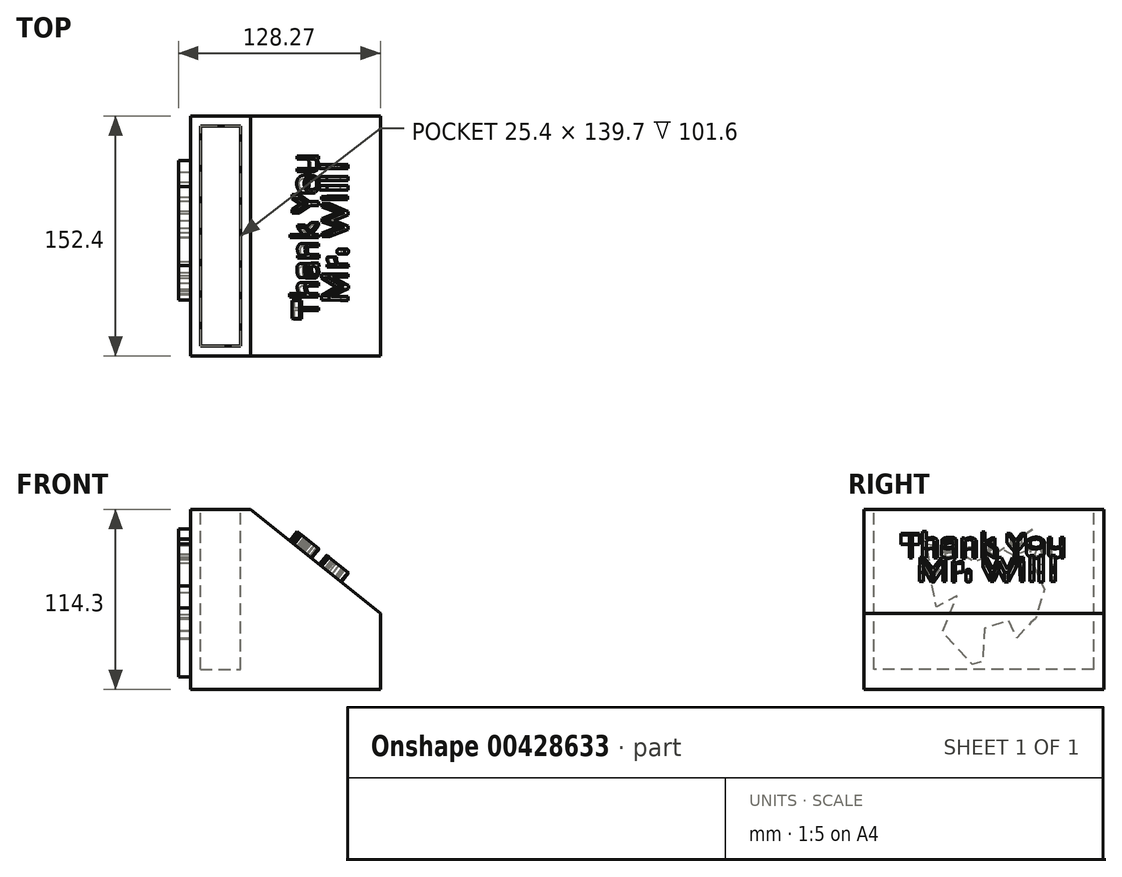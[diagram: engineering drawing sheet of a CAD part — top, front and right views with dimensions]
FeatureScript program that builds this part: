
annotation { "Feature Type Name" : "Feature", "Feature Type Description" : "" }
export const myFeature = defineFeature(function(context is Context, id is Id, definition is map)
    precondition{}
    {
        {
            var Q0;
            Q0=qCreatedBy(makeId("Front.planeOp"),FACE);
            var sketch = newSketch(context, id + "F0", { "sketchPlane" : qUnion([Q0])});
            skLineSegment(sketch, "E0.bottom", {"start": v(-51.92, 36.98) * mm, "end": v(-13.82, 36.98) * mm});
            skLineSegment(sketch, "E0.top", {"start": v(-51.92, -77.32) * mm, "end": v(-13.82, -77.32) * mm});
            skLineSegment(sketch, "E0.left", {"start": v(-51.92, 36.98) * mm, "end": v(-51.92, -77.32) * mm});
            skLineSegment(sketch, "E0.right", {"start": v(-13.82, 36.98) * mm, "end": v(-13.82, -77.32) * mm});
            skLineSegment(sketch, "E1", {"start": v(68.73, -77.32) * mm, "end": v(-13.82, -77.32) * mm});
            skLineSegment(sketch, "E2", {"start": v(68.73, -77.32) * mm, "end": v(68.73, -29.16) * mm});
            skLineSegment(sketch, "E3", {"start": v(68.73, -29.16) * mm, "end": v(-13.82, 36.98) * mm});
            skSolve(sketch);
        }
        {
            var Q0;
            Q0=makeQuery(id+"F0.imprint","IMPRINT",FACE,{"disambiguationData":[TD([[makeQuery(id+"F0.imprint","IMPRINT",EDGE,{"derivedFrom":sQuery(id+"F0.wireOp",EDGE,"E0.bottom")}),-1.0]])]});
            var Q1;
            Q1=makeQuery(id+"F0.imprint","IMPRINT",FACE,{"disambiguationData":[TD([[makeQuery(id+"F0.imprint","IMPRINT",EDGE,{"derivedFrom":sQuery(id+"F0.wireOp",EDGE,"E0.right")}),1.0]])]});
            extrude(context, id + "F1", {"entities" : qUnion([Q0, Q1]), "depth" : 152.4 * mm});
        }
        {
            var Q0;
            Q0=makeQuery(id+"F1.opExtrude","SWEPT_FACE",FACE,{"disambiguationData":[OSD([sQuery(id+"F0.wireOp",EDGE,"E0.bottom")])]});
            var sketch = newSketch(context, id + "F2", { "sketchPlane" : qUnion([Q0])});
            skLineSegment(sketch, "E4", {"start": v(-51.92, 0) * mm, "end": v(-51.92, -50.8) * mm});
            skPoint(sketch, "E5.centerSnap0", {"position": v(-32.87, 0) * mm});
            skPoint(sketch, "E5.centerSnap1", {"position": v(-51.92, -25.4) * mm});
            skLineSegment(sketch, "E6", {"start": v(-51.92, -50.8) * mm, "end": v(-51.92, -101.6) * mm});
            skPoint(sketch, "E7.centerSnap0", {"position": v(-51.92, -76.2) * mm});
            skLineSegment(sketch, "E8", {"start": v(-51.92, -101.6) * mm, "end": v(-51.92, -152.4) * mm});
            skPoint(sketch, "E9.centerSnap0", {"position": v(-51.92, -127) * mm});
            skPoint(sketch, "E10.startSnap0", {"position": v(-32.87, -152.4) * mm});
            skLineSegment(sketch, "E11", {"start": v(-45.57, -6.35) * mm, "end": v(-45.57, -146.05) * mm});
            skLineSegment(sketch, "E12", {"start": v(-20.17, -146.05) * mm, "end": v(-20.17, -6.35) * mm});
            skLineSegment(sketch, "E13", {"start": v(-45.57, -6.35) * mm, "end": v(-20.17, -6.35) * mm});
            skLineSegment(sketch, "E14", {"start": v(-45.57, -146.05) * mm, "end": v(-20.17, -146.05) * mm});
            skSolve(sketch);
        }
        {
            var Q0;
            Q0=makeQuery(id+"F1.opExtrude","SWEPT_FACE",FACE,{"disambiguationData":[OSD([sQuery(id+"F0.wireOp",EDGE,"E3")])]});
            var sketch = newSketch(context, id + "F3", { "sketchPlane" : qUnion([Q0])});
            skLineSegment(sketch, "E15", {"start": v(0, -128.67) * mm, "end": v(0, -117.04) * mm});
            skLineSegment(sketch, "E16", {"start": v(0, -117.04) * mm, "end": v(1.55, -117.04) * mm});
            skLineSegment(sketch, "E17", {"start": v(1.55, -117.04) * mm, "end": v(1.55, -121.65) * mm});
            skLineSegment(sketch, "E18", {"start": v(1.55, -121.65) * mm, "end": v(15.42, -121.65) * mm});
            skLineSegment(sketch, "E19", {"start": v(15.42, -121.65) * mm, "end": v(15.42, -123.54) * mm});
            skLineSegment(sketch, "E20", {"start": v(15.42, -123.54) * mm, "end": v(1.55, -123.54) * mm});
            skLineSegment(sketch, "E21", {"start": v(1.55, -123.54) * mm, "end": v(1.55, -128.78) * mm});
            skLineSegment(sketch, "E22", {"start": v(1.55, -128.78) * mm, "end": v(0, -128.67) * mm});
            skLineSegment(sketch, "E23", {"start": v(-1.97, -115.05) * mm, "end": v(15.11, -115.05) * mm});
            skLineSegment(sketch, "E24", {"start": v(15.11, -115.05) * mm, "end": v(15.11, -112.72) * mm});
            skFitSpline(sketch, "E25", {"points": [v(5.82, -112.75) * mm, v(4.64, -111.39) * mm, v(4.22, -109.92) * mm, v(4.22, -107.83) * mm, v(5.92, -106.05) * mm, v(7.53, -105.73) * mm], "startDerivative": vector(-5.14, 7.22) * mm, "endDerivative": vector(8.33, 0.38) * mm});
            skLineSegment(sketch, "E26", {"start": v(7.85, -112.75) * mm, "end": v(15.11, -112.75) * mm});
            skLineSegment(sketch, "E27", {"start": v(-1.97, -115.05) * mm, "end": v(-1.97, -112.65) * mm});
            skLineSegment(sketch, "E28", {"start": v(-1.97, -112.65) * mm, "end": v(5.82, -112.75) * mm});
            skLineSegment(sketch, "E29", {"start": v(7.53, -105.73) * mm, "end": v(15.53, -105.73) * mm});
            skLineSegment(sketch, "E30", {"start": v(15.53, -105.73) * mm, "end": v(15.53, -107.93) * mm});
            skLineSegment(sketch, "E31", {"start": v(15.53, -107.93) * mm, "end": v(7.53, -107.93) * mm});
            skFitSpline(sketch, "E32", {"points": [v(7.85, -112.75) * mm, v(6.56, -111.5) * mm, v(5.82, -109.5) * mm, v(7.53, -107.93) * mm], "startDerivative": vector(-3.95, 3.77) * mm, "endDerivative": vector(7.86, 4.5) * mm});
            skLineSegment(sketch, "E33", {"start": v(8.58, -75.32) * mm, "end": v(4.47, -70.95) * mm});
            skLineSegment(sketch, "E34", {"start": v(4.47, -70.95) * mm, "end": v(4.47, -69.17) * mm});
            skLineSegment(sketch, "E35", {"start": v(8.58, -73.2) * mm, "end": v(4.47, -69.17) * mm});
            skLineSegment(sketch, "E36", {"start": v(8.58, -73.2) * mm, "end": v(15.22, -67.5) * mm});
            skLineSegment(sketch, "E37", {"start": v(15.22, -67.5) * mm, "end": v(15.22, -69.43) * mm});
            skLineSegment(sketch, "E38", {"start": v(15.22, -69.43) * mm, "end": v(9.52, -75.23) * mm});
            skLineSegment(sketch, "E39", {"start": v(9.52, -75.23) * mm, "end": v(15.52, -75.23) * mm});
            skLineSegment(sketch, "E40", {"start": v(15.52, -75.23) * mm, "end": v(15.52, -77.3) * mm});
            skLineSegment(sketch, "E41", {"start": v(15.52, -77.3) * mm, "end": v(-1.78, -77.3) * mm});
            skLineSegment(sketch, "E42", {"start": v(-1.78, -77.3) * mm, "end": v(-1.78, -75.32) * mm});
            skLineSegment(sketch, "E43", {"start": v(4.36, -90.13) * mm, "end": v(15.63, -90.13) * mm});
            skLineSegment(sketch, "E44", {"start": v(15.63, -90.13) * mm, "end": v(15.63, -87.94) * mm});
            skLineSegment(sketch, "E45", {"start": v(15.63, -87.94) * mm, "end": v(8.58, -87.94) * mm});
            skLineSegment(sketch, "E46", {"start": v(4.36, -90.13) * mm, "end": v(4.36, -88.49) * mm});
            skLineSegment(sketch, "E47", {"start": v(4.36, -88.49) * mm, "end": v(5.7, -88.49) * mm});
            skFitSpline(sketch, "E48", {"points": [v(5.7, -88.49) * mm, v(4.7, -86.62) * mm, v(4.25, -84.1) * mm, v(5.7, -81.7) * mm, v(7.49, -80.81) * mm], "startDerivative": vector(-4.46, 7.44) * mm, "endDerivative": vector(7.96, 2.67) * mm});
            skLineSegment(sketch, "E49", {"start": v(7.49, -80.81) * mm, "end": v(15.52, -80.81) * mm});
            skPoint(sketch, "E49.endSnap0", {"position": v(15.52, -76.27) * mm});
            skLineSegment(sketch, "E50", {"start": v(15.52, -80.81) * mm, "end": v(15.52, -83) * mm});
            skLineSegment(sketch, "E51", {"start": v(15.52, -83) * mm, "end": v(7.49, -83) * mm});
            skFitSpline(sketch, "E52", {"points": [v(7.49, -83) * mm, v(6.6, -84) * mm, v(6.26, -85.42) * mm, v(8.58, -87.94) * mm], "startDerivative": vector(-3.47, -3.28) * mm, "endDerivative": vector(11.5, -2.26) * mm});
            skFitSpline(sketch, "E53", {"points": [v(5.59, -102.51) * mm, v(4.82, -101.63) * mm, v(4.25, -100.1) * mm, v(4.14, -95.61) * mm, v(6.26, -93.53) * mm], "startDerivative": vector(-0.62, 6.93) * mm, "endDerivative": vector(8.79, 5.04) * mm});
            skFitSpline(sketch, "E54", {"points": [v(5.59, -102.51) * mm, v(6.82, -102.51) * mm, v(6.06, -100.44) * mm, v(5.59, -98.46) * mm, v(6.37, -96.05) * mm, v(8.38, -95.94) * mm, v(8.6, -99.89) * mm, v(10.45, -102.51) * mm, v(12.62, -102.96) * mm, v(15.3, -100.76) * mm, v(15.41, -97.37) * mm, v(14.4, -95.5) * mm], "startDerivative": vector(28.37, -7.23) * mm, "endDerivative": vector(-13.83, 20.1) * mm});
            skLineSegment(sketch, "E55", {"start": v(14.4, -95.5) * mm, "end": v(15.63, -95.5) * mm});
            skLineSegment(sketch, "E56", {"start": v(15.63, -95.5) * mm, "end": v(15.41, -93.42) * mm});
            skLineSegment(sketch, "E57", {"start": v(15.41, -93.42) * mm, "end": v(6.26, -93.53) * mm});
            skLineSegment(sketch, "E58", {"start": v(0, -61.47) * mm, "end": v(0, -59.24) * mm});
            skLineSegment(sketch, "E59", {"start": v(0, -52.37) * mm, "end": v(0, -49.75) * mm});
            skLineSegment(sketch, "E60", {"start": v(0, -49.75) * mm, "end": v(8.14, -54.4) * mm});
            skLineSegment(sketch, "E61", {"start": v(8.14, -54.4) * mm, "end": v(15.33, -54.4) * mm});
            skLineSegment(sketch, "E62", {"start": v(15.33, -54.4) * mm, "end": v(15.33, -56.72) * mm});
            skLineSegment(sketch, "E63", {"start": v(15.33, -56.72) * mm, "end": v(9.03, -56.72) * mm});
            skLineSegment(sketch, "E64", {"start": v(9.03, -56.72) * mm, "end": v(0, -61.47) * mm});
            skLineSegment(sketch, "E65", {"start": v(0, -59.24) * mm, "end": v(6.95, -55.75) * mm});
            skLineSegment(sketch, "E66", {"start": v(6.95, -55.75) * mm, "end": v(0, -52.37) * mm});
            skFitSpline(sketch, "E67", {"points": [v(5.77, -42.88) * mm, v(6.07, -41.14) * mm, v(8.63, -39.78) * mm, v(12.28, -40.07) * mm, v(13.76, -41.81) * mm, v(13.66, -44.72) * mm, v(12.08, -46.17) * mm, v(8.73, -46.56) * mm, v(6.26, -45.1) * mm, v(5.77, -42.88) * mm]});
            skFitSpline(sketch, "E68", {"points": [v(3.7, -43.36) * mm, v(4.59, -39.97) * mm, v(7.74, -37.84) * mm, v(11.69, -37.94) * mm, v(14.55, -39.59) * mm, v(15.63, -42.5) * mm, v(15.43, -45.78) * mm, v(13.36, -47.82) * mm, v(10.7, -48.98) * mm, v(5.77, -47.62) * mm, v(3.7, -43.36) * mm]});
            skLineSegment(sketch, "E69", {"start": v(4.19, -35.27) * mm, "end": v(4.19, -33.29) * mm});
            skLineSegment(sketch, "E70", {"start": v(4.19, -27.45) * mm, "end": v(4.19, -25.43) * mm});
            skLineSegment(sketch, "E71", {"start": v(4.19, -25.43) * mm, "end": v(15.48, -25.43) * mm});
            skLineSegment(sketch, "E72", {"start": v(15.48, -25.43) * mm, "end": v(15.48, -27.35) * mm});
            skLineSegment(sketch, "E73", {"start": v(15.48, -27.35) * mm, "end": v(14.08, -27.36) * mm});
            skLineSegment(sketch, "E74", {"start": v(4.19, -33.29) * mm, "end": v(11.9, -33.29) * mm});
            skLineSegment(sketch, "E75", {"start": v(4.19, -35.27) * mm, "end": v(11.6, -35.27) * mm});
            skFitSpline(sketch, "E76", {"points": [v(11.6, -35.27) * mm, v(13.96, -34.36) * mm, v(15.22, -32.8) * mm, v(15.47, -30.31) * mm, v(14.08, -27.36) * mm], "startDerivative": vector(10.28, 2.9) * mm, "endDerivative": vector(-8.16, 8.85) * mm});
            skLineSegment(sketch, "E77", {"start": v(4.19, -27.45) * mm, "end": v(11.9, -27.45) * mm});
            skLineSegment(sketch, "E78", {"start": v(24.1, -116.78) * mm, "end": v(24.1, -114.12) * mm});
            skLineSegment(sketch, "E79", {"start": v(24.1, -114.12) * mm, "end": v(35.64, -108.52) * mm});
            skLineSegment(sketch, "E80", {"start": v(35.64, -108.52) * mm, "end": v(24.1, -102.97) * mm});
            skLineSegment(sketch, "E81", {"start": v(24.1, -102.97) * mm, "end": v(24.1, -100.38) * mm});
            skLineSegment(sketch, "E82", {"start": v(24.1, -100.38) * mm, "end": v(39.36, -100.38) * mm});
            skLineSegment(sketch, "E83", {"start": v(39.36, -100.38) * mm, "end": v(39.36, -102.15) * mm});
            skLineSegment(sketch, "E84", {"start": v(39.36, -102.15) * mm, "end": v(26.62, -102.15) * mm});
            skLineSegment(sketch, "E85", {"start": v(26.62, -102.15) * mm, "end": v(39.84, -107.7) * mm});
            skLineSegment(sketch, "E86", {"start": v(39.84, -107.7) * mm, "end": v(39.96, -109.58) * mm});
            skLineSegment(sketch, "E87", {"start": v(39.96, -109.58) * mm, "end": v(26.14, -114.65) * mm});
            skLineSegment(sketch, "E88", {"start": v(26.14, -114.65) * mm, "end": v(39.4, -114.65) * mm});
            skLineSegment(sketch, "E89", {"start": v(39.4, -114.65) * mm, "end": v(39.36, -117.01) * mm});
            skLineSegment(sketch, "E90", {"start": v(39.36, -117.01) * mm, "end": v(24.1, -116.78) * mm});
            skLineSegment(sketch, "E91", {"start": v(28.43, -96.01) * mm, "end": v(28.43, -94.36) * mm});
            skLineSegment(sketch, "E92", {"start": v(28.43, -96.01) * mm, "end": v(39.72, -96.01) * mm});
            skLineSegment(sketch, "E93", {"start": v(39.72, -96.01) * mm, "end": v(39.6, -94.12) * mm});
            skLineSegment(sketch, "E94", {"start": v(39.6, -94.12) * mm, "end": v(32.03, -94.12) * mm});
            skFitSpline(sketch, "E95", {"points": [v(32.03, -94.12) * mm, v(30.35, -92.35) * mm, v(29.87, -89.64) * mm, v(28.79, -89.64) * mm, v(28.55, -91.53) * mm, v(29.87, -94.12) * mm, v(28.43, -94.36) * mm], "startDerivative": vector(-13, 7.92) * mm, "endDerivative": vector(-15.62, 0.33) * mm});
            skCircle(sketch, "E96", {"center": v(38.16, -85.98) * mm, "radius": 1.67 * mm});
            skLineSegment(sketch, "E97", {"start": v(39.24, -72.06) * mm, "end": v(39.36, -69.7) * mm});
            skLineSegment(sketch, "E98", {"start": v(39.36, -69.7) * mm, "end": v(27.95, -66.52) * mm});
            skLineSegment(sketch, "E99", {"start": v(27.95, -66.52) * mm, "end": v(39.48, -62.98) * mm});
            skLineSegment(sketch, "E100", {"start": v(39.48, -62.98) * mm, "end": v(39.48, -60.62) * mm});
            skLineSegment(sketch, "E101", {"start": v(39.48, -60.62) * mm, "end": v(24.22, -55.5) * mm});
            skLineSegment(sketch, "E102", {"start": v(24.22, -55.5) * mm, "end": v(24.22, -57.9) * mm});
            skLineSegment(sketch, "E103", {"start": v(24.22, -57.9) * mm, "end": v(36.72, -61.2) * mm});
            skLineSegment(sketch, "E104", {"start": v(36.72, -61.2) * mm, "end": v(24.22, -65.13) * mm});
            skLineSegment(sketch, "E105", {"start": v(24.22, -65.13) * mm, "end": v(24.22, -67.21) * mm});
            skLineSegment(sketch, "E106", {"start": v(24.22, -67.21) * mm, "end": v(36.72, -70.53) * mm});
            skLineSegment(sketch, "E107", {"start": v(36.72, -70.53) * mm, "end": v(24.22, -74.18) * mm});
            skLineSegment(sketch, "E108", {"start": v(24.22, -74.18) * mm, "end": v(24.34, -76.66) * mm});
            skLineSegment(sketch, "E109", {"start": v(24.34, -76.66) * mm, "end": v(39.24, -72.06) * mm});
            skLineSegment(sketch, "E110", {"start": v(28.4, -53.14) * mm, "end": v(28.4, -50.8) * mm});
            skLineSegment(sketch, "E111", {"start": v(28.4, -50.8) * mm, "end": v(39.14, -50.8) * mm});
            skLineSegment(sketch, "E112", {"start": v(39.14, -50.8) * mm, "end": v(39.14, -53.08) * mm});
            skLineSegment(sketch, "E113", {"start": v(39.14, -53.08) * mm, "end": v(28.4, -53.14) * mm});
            skLineSegment(sketch, "E114", {"start": v(24.09, -53.14) * mm, "end": v(26.3, -53.14) * mm});
            skLineSegment(sketch, "E115", {"start": v(26.3, -53.14) * mm, "end": v(26.3, -51.16) * mm});
            skLineSegment(sketch, "E116", {"start": v(26.3, -51.16) * mm, "end": v(24.06, -51.16) * mm});
            skLineSegment(sketch, "E117", {"start": v(24.06, -51.16) * mm, "end": v(24.09, -53.14) * mm});
            skLineSegment(sketch, "E118", {"start": v(22.2, -46.98) * mm, "end": v(39.36, -46.98) * mm});
            skLineSegment(sketch, "E119", {"start": v(39.36, -46.98) * mm, "end": v(39.36, -44.28) * mm});
            skLineSegment(sketch, "E120", {"start": v(39.36, -44.28) * mm, "end": v(22.2, -44.28) * mm});
            skLineSegment(sketch, "E121", {"start": v(22.2, -44.28) * mm, "end": v(22.2, -46.98) * mm});
            skLineSegment(sketch, "E122", {"start": v(22.2, -46.98) * mm, "end": v(22.2, -46.98) * mm});
            skLineSegment(sketch, "E123", {"start": v(22.17, -41.09) * mm, "end": v(39.55, -41.09) * mm});
            skLineSegment(sketch, "E124", {"start": v(39.55, -41.09) * mm, "end": v(39.55, -38.48) * mm});
            skLineSegment(sketch, "E125", {"start": v(39.55, -38.48) * mm, "end": v(22.07, -38.48) * mm});
            skLineSegment(sketch, "E126", {"start": v(22.07, -38.48) * mm, "end": v(22.17, -41.09) * mm});
            skLineSegment(sketch, "E127", {"start": v(22.17, -33.4) * mm, "end": v(34.65, -33.4) * mm});
            skLineSegment(sketch, "E128", {"start": v(34.65, -33.4) * mm, "end": v(34.65, -30.84) * mm});
            skLineSegment(sketch, "E129", {"start": v(34.65, -30.84) * mm, "end": v(22.17, -30.84) * mm});
            skLineSegment(sketch, "E130", {"start": v(22.17, -30.84) * mm, "end": v(22.17, -33.4) * mm});
            skLineSegment(sketch, "E131", {"start": v(36.5, -33.4) * mm, "end": v(39.42, -33.4) * mm});
            skLineSegment(sketch, "E132", {"start": v(39.42, -33.4) * mm, "end": v(39.42, -30.69) * mm});
            skLineSegment(sketch, "E133", {"start": v(39.42, -30.69) * mm, "end": v(36.52, -30.69) * mm});
            skLineSegment(sketch, "E134", {"start": v(36.52, -30.69) * mm, "end": v(36.5, -33.4) * mm});
            skFitSpline(sketch, "E135", {"points": [v(10.27, -99.74) * mm, v(10.24, -95.75) * mm, v(12.54, -95.73) * mm, v(13.9, -97.32) * mm, v(13.67, -100.4) * mm, v(11.94, -100.69) * mm, v(10.27, -99.74) * mm]});
            skFitSpline(sketch, "E136", {"points": [v(11.9, -33.29) * mm, v(12.3, -33.29) * mm, v(12.84, -33.09) * mm, v(13.44, -32.56) * mm, v(13.88, -31.36) * mm, v(13.9, -29.65) * mm, v(13.39, -28.36) * mm, v(12.84, -27.84) * mm, v(11.9, -27.45) * mm], "startDerivative": vector(4.67, -0.39) * mm, "endDerivative": vector(-9.65, 4.45) * mm});
            skLineSegment(sketch, "E137", {"start": v(-1.78, -75.32) * mm, "end": v(8.58, -75.32) * mm});
            skSolve(sketch);
        }
        {
            var Q0;
            Q0=makeQuery(id+"F3.imprint","IMPRINT",FACE,{"disambiguationData":[TD([[makeQuery(id+"F3.imprint","IMPRINT",EDGE,{"derivedFrom":sQuery(id+"F3.wireOp",EDGE,"E15")}),-1.0]])]});
            var Q1;
            Q1=makeQuery(id+"F3.imprint","IMPRINT",FACE,{"disambiguationData":[TD([[makeQuery(id+"F3.imprint","IMPRINT",EDGE,{"derivedFrom":sQuery(id+"F3.wireOp",EDGE,"E53")}),-1.0]])]});
            var Q2;
            Q2=makeQuery(id+"F3.imprint","IMPRINT",FACE,{"disambiguationData":[TD([[makeQuery(id+"F3.imprint","IMPRINT",EDGE,{"derivedFrom":sQuery(id+"F3.wireOp",EDGE,"E43")}),1.0]])]});
            var Q3;
            Q3=makeQuery(id+"F3.imprint","IMPRINT",FACE,{"disambiguationData":[TD([[makeQuery(id+"F3.imprint","IMPRINT",EDGE,{"derivedFrom":sQuery(id+"F3.wireOp",EDGE,"E58")}),-1.0]])]});
            var Q4;
            Q4=makeQuery(id+"F3.imprint","IMPRINT",FACE,{"disambiguationData":[TD([[makeQuery(id+"F3.imprint","IMPRINT",EDGE,{"derivedFrom":sQuery(id+"F3.wireOp",EDGE,"E67")}),1.0]])]});
            var Q5;
            Q5=makeQuery(id+"F3.imprint","IMPRINT",FACE,{"disambiguationData":[TD([[makeQuery(id+"F3.imprint","IMPRINT",EDGE,{"derivedFrom":sQuery(id+"F3.wireOp",EDGE,"E97")}),1.0]])]});
            var Q6;
            Q6=makeQuery(id+"F3.imprint","IMPRINT",FACE,{"disambiguationData":[TD([[makeQuery(id+"F3.imprint","IMPRINT",EDGE,{"derivedFrom":sQuery(id+"F3.wireOp",EDGE,"E110")}),-1.0]])]});
            var Q7;
            Q7=makeQuery(id+"F3.imprint","IMPRINT",FACE,{"disambiguationData":[TD([[makeQuery(id+"F3.imprint","IMPRINT",EDGE,{"derivedFrom":sQuery(id+"F3.wireOp",EDGE,"E114")}),1.0]])]});
            var Q8;
            Q8=makeQuery(id+"F3.imprint","IMPRINT",FACE,{"disambiguationData":[TD([[makeQuery(id+"F3.imprint","IMPRINT",EDGE,{"derivedFrom":sQuery(id+"F3.wireOp",EDGE,"E118")}),1.0]])]});
            var Q9;
            Q9=makeQuery(id+"F3.imprint","IMPRINT",FACE,{"disambiguationData":[TD([[makeQuery(id+"F3.imprint","IMPRINT",EDGE,{"derivedFrom":sQuery(id+"F3.wireOp",EDGE,"E123")}),1.0]])]});
            var Q10;
            Q10=makeQuery(id+"F3.imprint","IMPRINT",FACE,{"disambiguationData":[TD([[makeQuery(id+"F3.imprint","IMPRINT",EDGE,{"derivedFrom":sQuery(id+"F3.wireOp",EDGE,"E127")}),1.0]])]});
            var Q11;
            Q11=makeQuery(id+"F3.imprint","IMPRINT",FACE,{"disambiguationData":[TD([[makeQuery(id+"F3.imprint","IMPRINT",EDGE,{"derivedFrom":sQuery(id+"F3.wireOp",EDGE,"E131")}),1.0]])]});
            var Q12;
            Q12=makeQuery(id+"F3.imprint","IMPRINT",FACE,{"disambiguationData":[TD([[makeQuery(id+"F3.imprint","IMPRINT",EDGE,{"derivedFrom":sQuery(id+"F3.wireOp",EDGE,"E96")}),1.0]])]});
            var Q13;
            Q13=makeQuery(id+"F3.imprint","IMPRINT",FACE,{"disambiguationData":[TD([[makeQuery(id+"F3.imprint","IMPRINT",EDGE,{"derivedFrom":sQuery(id+"F3.wireOp",EDGE,"E91")}),-1.0]])]});
            var Q14;
            Q14=makeQuery(id+"F3.imprint","IMPRINT",FACE,{"disambiguationData":[TD([[makeQuery(id+"F3.imprint","IMPRINT",EDGE,{"derivedFrom":sQuery(id+"F3.wireOp",EDGE,"E78")}),-1.0]])]});
            var Q15;
            {var subQ2=sQuery(id+"F3.wireOp",EDGE,"E23");Q15=makeQuery(id+"F3.imprint","IMPRINT",FACE,{"disambiguationData":[TD([[makeQuery(id+"F3.imprint","IMPRINT",EDGE,{"derivedFrom":subQ2}),1.0]])]});}
            var Q16;
            Q16=makeQuery(id+"F3.imprint","IMPRINT",FACE,{"disambiguationData":[TD([[makeQuery(id+"F3.imprint","IMPRINT",EDGE,{"derivedFrom":sQuery(id+"F3.wireOp",EDGE,"E69")}),-1.0]])]});
            var Q17;
            Q17=makeQuery(id+"F3.imprint","IMPRINT",FACE,{"disambiguationData":[TD([[makeQuery(id+"F3.imprint","IMPRINT",EDGE,{"derivedFrom":sQuery(id+"F3.wireOp",EDGE,"E33")}),-1.0]])]});
            extrude(context, id + "F4", {"entities" : qUnion([Q0, Q1, Q2, Q3, Q4, Q5, Q6, Q7, Q8, Q9, Q10, Q11, Q12, Q13, Q14, Q15, Q16, Q17]), "operationType" : NewBodyOperationType.ADD, "depth" : 7.62 * mm});
        }
        {
            var Q0;
            Q0=makeQuery(id+"FcFQkPFWr5uKpiW_1.boolean.opBoolean","MERGE",FACE,{"derivedFrom":[makeQuery(id+"F1.opExtrude","SWEPT_FACE",FACE,{"disambiguationData":[OSD([sQuery(id+"F0.wireOp",EDGE,"E0.left")])]}),makeQuery(id+"FcFQkPFWr5uKpiW_1.opExtrude","SWEPT_FACE",FACE,{"disambiguationData":[OSD([sQuery(id+"F0.wireOp",EDGE,"MClin2kA-0iJw-wpdR-LezF-TghjcDfDoHo2")])]})]});
            var sketch = newSketch(context, id + "F5", { "sketchPlane" : qUnion([Q0])});
            skFitSpline(sketch, "E138", {"points": [v(45.27, 24.35) * mm, v(44.91, 22.74) * mm, v(48.32, 21.3) * mm, v(54.96, 18.88) * mm, v(63.04, 12.15) * mm, v(66, 9.36) * mm, v(66.18, 8.38) * mm, v(64.66, 8.65) * mm, v(62.86, 8.65) * mm, v(60.89, 6.94) * mm, v(58.46, 6.85) * mm, v(55.41, 8.92) * mm, v(46.8, 13.5) * mm, v(37.46, 16.81) * mm, v(31.99, 17.53) * mm, v(28.3, 17.26) * mm, v(30.28, 15.1) * mm, v(33.24, 14.03) * mm, v(38.45, 14.12) * mm, v(43.2, 13.13) * mm, v(52.9, 8.47) * mm, v(53.8, 6.85) * mm, v(51.2, 6.85) * mm, v(45.99, 4.25) * mm, v(43.56, 0) * mm, v(41.95, -4.28) * mm, v(41.86, -6.97) * mm, v(40.28, -9.98) * mm, v(37.11, -15.11) * mm, v(35.6, -22.96) * mm, v(36.59, -27.8) * mm, v(39.6, -32.02) * mm, v(44.96, -32.25) * mm, v(48.2, -30.44) * mm, v(50.25, -29.6) * mm, v(51.45, -30.28) * mm, v(49.42, -32.62) * mm, v(47.23, -33.9) * mm, v(45.8, -36.1) * mm, v(45.42, -40.02) * mm, v(47.83, -43.95) * mm, v(49.74, -45.18) * mm, v(54.55, -45) * mm, v(55, -44.6) * mm, v(59.08, -44.42) * mm, v(60.07, -39.93) * mm, v(61.32, -40.07) * mm, v(61.77, -37.82) * mm, v(60.65, -36.2) * mm, v(60.96, -32.75) * mm, v(71.82, -31.94) * mm, v(76.94, -33.6) * mm, v(77.2, -35.27) * mm, v(76.18, -37.87) * mm, v(74.38, -42.63) * mm, v(73.84, -45.59) * mm, v(74.88, -52.63) * mm, v(76.67, -57.88) * mm, v(76.27, -60.98) * mm, v(73.8, -65.96) * mm, v(71.06, -69.42) * mm, v(82.2, -62.2) * mm, v(88.47, -59.19) * mm, v(95.92, -53.35) * mm, v(101.76, -43.43) * mm, v(101.67, -30.02) * mm, v(94.4, -20.05) * mm, v(92.6, -19.78) * mm, v(92.7, -18.62) * mm, v(96.33, -16.06) * mm, v(101.13, -16.69) * mm, v(99.42, -19.24) * mm, v(103.01, -22.43) * mm, v(107.28, -25.44) * mm, v(110.82, -24.67) * mm, v(111, -19.96) * mm, v(112.26, -19.1) * mm, v(112, -15.16) * mm, v(107.32, -11.75) * mm, v(105.93, -11.57) * mm, v(112.57, -4.97) * mm, v(113.43, -2.15) * mm, v(112.48, -0.75) * mm, v(109.8, 0) * mm, v(112.93, 3.33) * mm, v(116.7, 10.47) * mm, v(116.07, 13.83) * mm, v(114.82, 15.04) * mm, v(110.35, 14.65) * mm, v(104.66, 11.18) * mm, v(94.98, 5.4) * mm, v(94.87, 12.06) * mm, v(93.6, 17.24) * mm, v(91.85, 18.27) * mm, v(87.17, 14.46) * mm, v(81.9, 3.45) * mm, v(80.96, 3.05) * mm, v(78.8, 5.17) * mm, v(75.85, 5.67) * mm, v(73.06, 6.55) * mm, v(70.86, 8.03) * mm, v(67.99, 9.69) * mm, v(58.56, 18.04) * mm, v(52, 22.26) * mm, v(45.27, 24.35) * mm]});
            skSolve(sketch);
        }
        {
            var Q0;
            Q0=makeQuery(id+"F5.imprint","IMPRINT",FACE,{"disambiguationData":[TD([[makeQuery(id+"F5.imprint","IMPRINT",EDGE,{"derivedFrom":sQuery(id+"F5.wireOp",EDGE,"E138")}),1.0]])]});
            extrude(context, id + "F6", {"entities" : qUnion([Q0]), "operationType" : NewBodyOperationType.ADD, "depth" : 7.62 * mm});
        }
        {
            var Q0;
            Q0=makeQuery(id+"F2.imprint","IMPRINT",FACE,{"disambiguationData":[TD([[makeQuery(id+"F2.imprint","IMPRINT",EDGE,{"derivedFrom":sQuery(id+"F2.wireOp",EDGE,"E11")}),1.0]])]});
            extrude(context, id + "F7", {"entities" : qUnion([Q0]), "operationType" : NewBodyOperationType.REMOVE, "oppositeDirection" : true, "depth" : 101.6 * mm});
        }
    });
